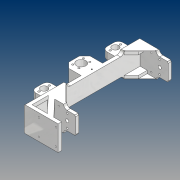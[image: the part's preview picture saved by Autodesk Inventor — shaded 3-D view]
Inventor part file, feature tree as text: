
AUTODESK INVENTOR PART (.ipt)
format: ipt  version: 2021 (Build 250183000, 183)  size: 491,008 bytes
history: native  units: mm
features: sketch x17, extrude x14, projected_geometry x13, fillet x3, mirror x3, chamfer x2, hole x2, other x2, reference x1
ambient origin geometry x8: Origin, YZ Plane, XZ Plane, XY Plane, X Axis, Y Axis, Z Axis, Center Point
bodies: Solid1 (feature_tree)
feature tree (57):
  extrude  "Extrusion1"  Depth=268.75mm
  extrude  "Extrusion2"  Depth=10.0mm
  extrude  "Extrusion3"  Depth=79.0mm TaperAngle=0.0deg
  fillet  "Fillet1"  Radius=45.0mm
  chamfer  "Chamfer1"  Distance=10.0mm
  mirror  "Mirror1"
  extrude  "Extrusion4"  Depth=2.0mm TaperAngle=45.0deg
  extrude  "Extrusion5"  Depth=36.5mm
  extrude  "Extrusion6"  TaperAngle=0.0deg  [1 undecoded]
  hole  "Hole2"  [1 undecoded]
  extrude  "Extrusion7"  Depth=10.0mm
  extrude  "Extrusion8"  Depth=55.5mm
  mirror  "Mirror2"
  extrude  "Extrusion9"  Depth=65.0mm
  hole  "Hole3"  [1 undecoded]
  sketch  "Sketch13"  dims[d41=47.35mm]
  extrude  "Extrusion10"  Depth=13.0mm
  chamfer  "Chamfer2"  Distance=10.0mm
  extrude  "Extrusion11"  Depth=50.0mm TaperAngle=0.0deg
  extrude  "Extrusion13"  Depth=13.0mm
  mirror  "Mirror5"
  fillet  "Fillet3"  Radius=5.0mm
  fillet  "Fillet4"  Radius=5.0mm
  extrude  "Extrusion14"  Depth=13.0mm
  extrude  "Extrusion15"  Depth=13.0mm TaperAngle=0.0deg
  sketch  "Sketch1"  dims[d0=50.0mm d1=268.75mm]
  sketch  "Sketch2"  dims[d2=10.0mm d3=0.0mm d5=250.0mm]
  projected_geometry  "Projected Loop1"
  sketch  "Sketch3"  dims[d6=251.0mm d7=79.0mm d8=0.0mm d9=45.0mm]
  projected_geometry  "Projected Loop2"
  sketch  "Sketch5"  dims[d10=45.0mm d11=10.0mm d12=0.0mm]
  sketch  "Sketch6"  dims[d13=10.0mm d14=2.0mm d15=2.0mm d16=45.0deg]
  projected_geometry  "Projected Loop3"
  sketch  "Sketch7"  dims[d26=36.5mm d27=5.2mm]
  projected_geometry  "Projected Loop4"
  sketch  "Sketch8"  dims[d28=9.0mm d29=0.0mm d30=0.0mm]
  sketch  "Sketch9"  dims[d31=65.0mm d32=10.0mm]
  projected_geometry  "Projected Loop5"
  sketch  "Sketch10"  dims[d33=10.0mm d34=40.0mm]
  projected_geometry  "Projected Loop6"
  sketch  "Sketch11"  dims[d35=55.5mm d36=0.0mm d37=55.0mm]
  projected_geometry  "Projected Loop7"
  sketch  "Sketch12"  dims[d38=10.0mm d39=0.0mm d40=65.0mm]
  projected_geometry  "Projected Loop8"
  sketch  "Sketch14"  dims[d42=4.2mm d43=6.0mm d44=4.0mm d45=2.0mm d46=90.0deg d47=8.0mm d48=20.594885mm d49=10.0mm]
  reference  "Reference4"
  sketch  "Sketch15"  dims[d50=144.0mm d51=0.0mm d52=13.0mm]
  projected_geometry  "Projected Loop9"
  projected_geometry  "Projected Loop10"
  sketch  "Sketch17"  dims[d53=43.0mm d54=10.0mm d55=0.0mm]
  projected_geometry  "Projected Loop13"
  sketch  "Sketch18"  dims[d56=60.0mm d57=50.0mm d58=0.0mm]
  projected_geometry  "Projected Loop14"
  sketch  "Sketch19"  dims[d59=40.0mm d60=26.0mm d61=6.0mm d62=4.0mm d63=2.0mm d64=90.0deg d65=12.5mm d66=20.594885mm d67=5.0mm d68=5.0mm d69=5.0mm d70=5.0mm d71=86.25mm d72=0.0mm d73=15.0mm d74=2.0mm d75=45.0deg d76=200.0mm d77=45.0mm d78=23.0mm d79=48.0mm d80=0.0mm d87=18.8mm d88=5.5mm d89=29.0mm d90=46.75mm d91=0.0mm d92=13.0mm d93=4.0mm d94=34.0mm d95=66.0mm d96=35.0mm d97=20.0mm d98=27.5mm d99=0.0mm d100=13.0mm d101=0.0mm]
  projected_geometry  "Projected Loop15"
  other  "0002_Part_Khop_tay_1.iam"
  other  "Dai_oc_truc_vit:1"
note: 3 required parameter values undecoded (feature->parameter linkage not recoverable at this tier; creation-order binding heuristic only, values carry confidence <= 0.55)
